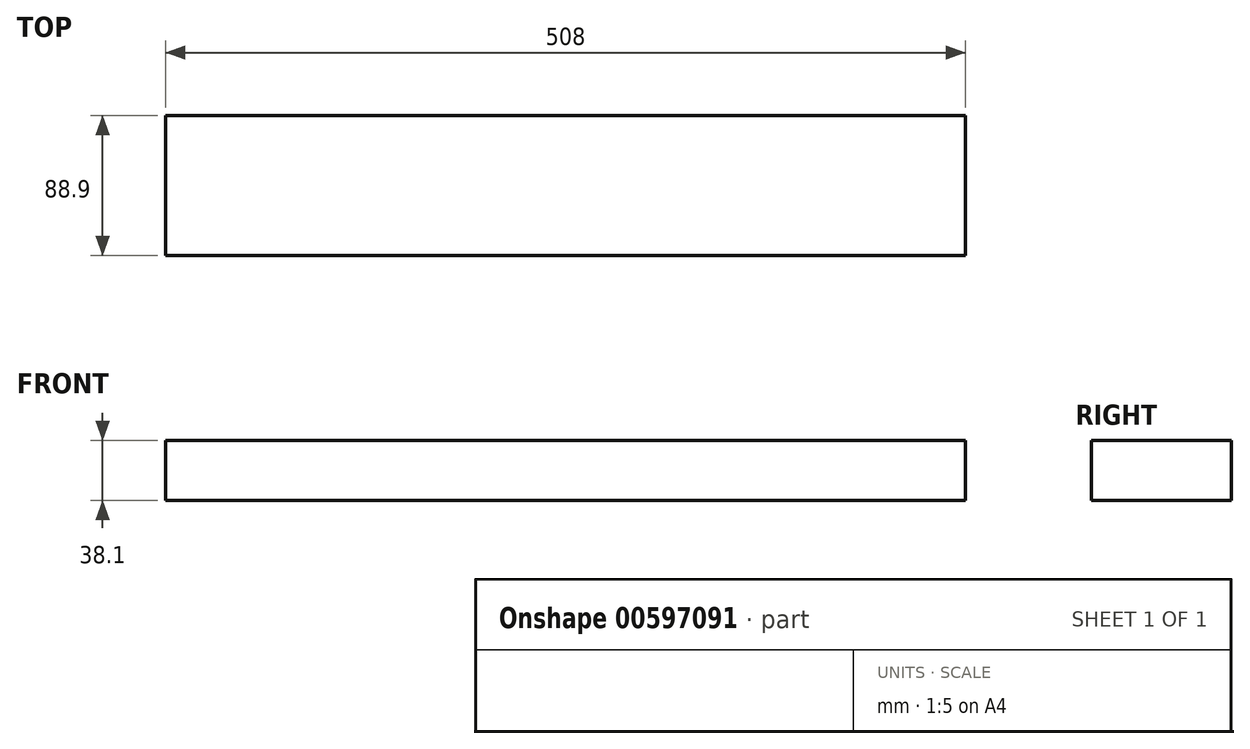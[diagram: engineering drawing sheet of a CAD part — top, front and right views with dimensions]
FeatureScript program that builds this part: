
annotation { "Feature Type Name" : "Feature", "Feature Type Description" : "" }
export const myFeature = defineFeature(function(context is Context, id is Id, definition is map)
    precondition{}
    {
        {
            var Q0;
            Q0=qCreatedBy(makeId("Top.planeOp"),FACE);
            var sketch = newSketch(context, id + "F0", { "sketchPlane" : qUnion([Q0])});
            skLineSegment(sketch, "E0.bottom", {"start": v(-141.11, 88.9) * mm, "end": v(366.89, 88.9) * mm});
            skLineSegment(sketch, "E0.top", {"start": v(-141.11, 0) * mm, "end": v(366.89, 0) * mm});
            skLineSegment(sketch, "E0.left", {"start": v(-141.11, 88.9) * mm, "end": v(-141.11, 0) * mm});
            skLineSegment(sketch, "E0.right", {"start": v(366.89, 88.9) * mm, "end": v(366.89, 0) * mm});
            skSolve(sketch);
        }
        {
            var Q0;
            Q0=makeQuery(id+"F0.imprint","IMPRINT",FACE,{"disambiguationData":[TD([[makeQuery(id+"F0.imprint","IMPRINT",EDGE,{"derivedFrom":sQuery(id+"F0.wireOp",EDGE,"E0.bottom")}),-1.0]])]});
            extrude(context, id + "F1", {"entities" : qUnion([Q0]), "depth" : 38.1 * mm, "offsetDistance" : 25.4 * mm});
        }
    });
